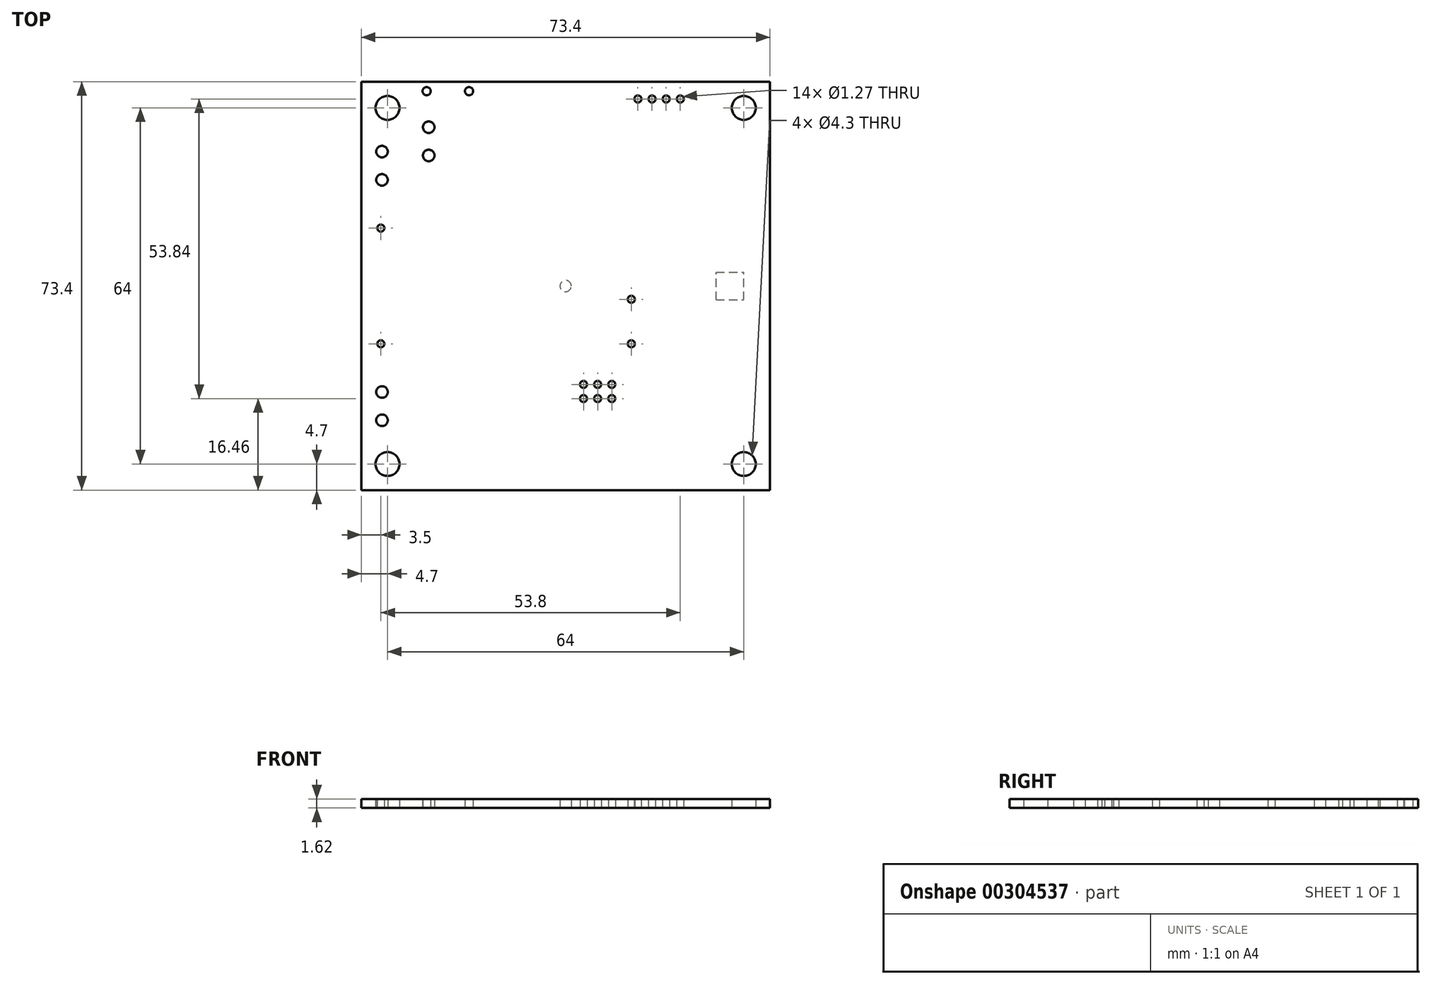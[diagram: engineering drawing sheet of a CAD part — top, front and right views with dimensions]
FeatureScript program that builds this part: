
annotation { "Feature Type Name" : "Feature", "Feature Type Description" : "" }
export const myFeature = defineFeature(function(context is Context, id is Id, definition is map)
    precondition{}
    {
        {
            var Q0;
            Q0=qCreatedBy(makeId("Top.planeOp"),FACE);
            var sketch = newSketch(context, id + "F0", { "sketchPlane" : qUnion([Q0])});
            skLineSegment(sketch, "E0.bottom", {"start": v(36.7, 36.7) * mm, "end": v(-36.7, 36.7) * mm});
            skLineSegment(sketch, "E0.top", {"start": v(36.7, -36.7) * mm, "end": v(-36.7, -36.7) * mm});
            skLineSegment(sketch, "E0.left", {"start": v(36.7, 36.7) * mm, "end": v(36.7, -36.7) * mm});
            skLineSegment(sketch, "E0.right", {"start": v(-36.7, 36.7) * mm, "end": v(-36.7, -36.7) * mm});
            skPoint(sketch, "E0.middle", {"position": v(0, 0) * mm});
            skCircle(sketch, "E1", {"center": v(-32, 32) * mm, "radius": 2.15 * mm});
            skCircle(sketch, "E2", {"center": v(32, 32) * mm, "radius": 2.15 * mm});
            skCircle(sketch, "E3", {"center": v(32, -32) * mm, "radius": 2.15 * mm});
            skCircle(sketch, "E4", {"center": v(-32, -32) * mm, "radius": 2.15 * mm});
            skLineSegment(sketch, "E5.bottom", {"start": v(32, 32) * mm, "end": v(-32, 32) * mm, "construction": true});
            skLineSegment(sketch, "E5.top", {"start": v(32, -32) * mm, "end": v(-32, -32) * mm, "construction": true});
            skLineSegment(sketch, "E5.left", {"start": v(32, 32) * mm, "end": v(32, -32) * mm, "construction": true});
            skLineSegment(sketch, "E5.right", {"start": v(-32, 32) * mm, "end": v(-32, -32) * mm, "construction": true});
            skSolve(sketch);
        }
        {
            var Q0;
            Q0 = qSketchRegion(id + "F0", true);
            extrude(context, id + "F1", {"entities" : qUnion([Q0]), "depth" : 1.57 * mm});
        }
        {
            var Q0;
            Q0=qCreatedBy(makeId("Top.planeOp"),FACE);
            var sketch = newSketch(context, id + "F2", { "sketchPlane" : qUnion([Q0])});
            skLineSegment(sketch, "E6", {"start": v(-33.2, 10.4) * mm, "end": v(-33.2, -10.4) * mm, "construction": true});
            skCircle(sketch, "E7", {"center": v(-33.2, -10.4) * mm, "radius": 0.64 * mm});
            skCircle(sketch, "E8", {"center": v(-33.2, 10.4) * mm, "radius": 0.64 * mm});
            skCircle(sketch, "E9", {"center": v(11.8, -10.4) * mm, "radius": 0.64 * mm});
            skCircle(sketch, "E10", {"center": v(11.8, -2.4) * mm, "radius": 0.64 * mm});
            skLineSegment(sketch, "E11", {"start": v(-33.2, -10.4) * mm, "end": v(11.8, -10.4) * mm, "construction": true});
            skLineSegment(sketch, "E12", {"start": v(11.8, -10.4) * mm, "end": v(11.8, -2.4) * mm, "construction": true});
            skSolve(sketch);
        }
        {
            var Q0;
            Q0 = qSketchRegion(id + "F2", true);
            extrude(context, id + "F3", {"entities" : qUnion([Q0]), "operationType" : NewBodyOperationType.REMOVE, "endBound" : BoundingType.THROUGH_ALL, "depth" : 25.4 * mm});
        }
        {
            var Q0;
            Q0=makeQuery(id+"F1.opExtrude","CAP_FACE",FACE,{"disambiguationData":[OSD([sQuery(id+"F0.wireOp",EDGE,"E0.bottom"),sQuery(id+"F0.wireOp",EDGE,"E0.top"),sQuery(id+"F0.wireOp",EDGE,"E0.left"),sQuery(id+"F0.wireOp",EDGE,"E0.right"),sQuery(id+"F0.wireOp",EDGE,"E1"),sQuery(id+"F0.wireOp",EDGE,"E2"),sQuery(id+"F0.wireOp",EDGE,"E3"),sQuery(id+"F0.wireOp",EDGE,"E4")])],"isStart":true});
            var sketch = newSketch(context, id + "F4", { "sketchPlane" : qUnion([Q0])});
            skLineSegment(sketch, "E13", {"start": v(0, 0) * mm, "end": v(29.53, 0) * mm, "construction": true});
            skLineSegment(sketch, "E14.bottom", {"start": v(27.03, 2.5) * mm, "end": v(32.03, 2.5) * mm});
            skLineSegment(sketch, "E14.top", {"start": v(27.03, -2.5) * mm, "end": v(32.03, -2.5) * mm});
            skLineSegment(sketch, "E14.left", {"start": v(27.03, 2.5) * mm, "end": v(27.03, -2.5) * mm});
            skLineSegment(sketch, "E14.right", {"start": v(32.03, 2.5) * mm, "end": v(32.03, -2.5) * mm});
            skPoint(sketch, "E14.middle", {"position": v(29.53, 0) * mm});
            skSolve(sketch);
        }
        {
            var Q0;
            Q0 = qSketchRegion(id + "F4", true);
            extrude(context, id + "F5", {"entities" : qUnion([Q0]), "operationType" : NewBodyOperationType.ADD, "depth" : 0.05 * mm});
        }
        {
            var Q0;
            Q0=qCreatedBy(makeId("Front.planeOp"),FACE);
            var sketch = newSketch(context, id + "F6", { "sketchPlane" : qUnion([Q0])});
            skLineSegment(sketch, "E15", {"start": v(0, 0) * mm, "end": v(0, -36.38) * mm, "construction": true});
            skSolve(sketch);
        }
        {
            var Q0;
            Q0=qCreatedBy(makeId("Top.planeOp"),FACE);
            var sketch = newSketch(context, id + "F7", { "sketchPlane" : qUnion([Q0])});
            skCircle(sketch, "E16", {"center": v(0, 0) * mm, "radius": 1.02 * mm});
            skSolve(sketch);
        }
        {
            var Q0;
            Q0=qCreatedBy(makeId("Top.planeOp"),FACE);
            var sketch = newSketch(context, id + "F8", { "sketchPlane" : qUnion([Q0])});
            skCircle(sketch, "E17", {"center": v(-24.97, 35) * mm, "radius": 0.74 * mm});
            skCircle(sketch, "E18", {"center": v(-17.35, 35) * mm, "radius": 0.74 * mm});
            skSolve(sketch);
        }
        {
            var Q0;
            Q0 = qSketchRegion(id + "F8", true);
            extrude(context, id + "F9", {"entities" : qUnion([Q0]), "operationType" : NewBodyOperationType.REMOVE, "endBound" : BoundingType.THROUGH_ALL, "depth" : 25.4 * mm});
        }
        {
            var Q0;
            Q0=qCreatedBy(makeId("Top.planeOp"),FACE);
            var sketch = newSketch(context, id + "F10", { "sketchPlane" : qUnion([Q0])});
            skCircle(sketch, "E19", {"center": v(-24.6, 28.53) * mm, "radius": 1.04 * mm});
            skCircle(sketch, "E20", {"center": v(-24.6, 23.45) * mm, "radius": 1.04 * mm});
            skCircle(sketch, "E21", {"center": v(-33, 24.14) * mm, "radius": 1.04 * mm});
            skCircle(sketch, "E22", {"center": v(-33, 19.06) * mm, "radius": 1.04 * mm});
            skCircle(sketch, "E23", {"center": v(-33, -19.06) * mm, "radius": 1.04 * mm});
            skCircle(sketch, "E24", {"center": v(-33, -24.14) * mm, "radius": 1.04 * mm});
            skSolve(sketch);
        }
        {
            var Q0;
            Q0 = qSketchRegion(id + "F10", true);
            extrude(context, id + "F11", {"entities" : qUnion([Q0]), "operationType" : NewBodyOperationType.REMOVE, "endBound" : BoundingType.THROUGH_ALL, "depth" : 25.4 * mm});
        }
        {
            var Q0;
            Q0 = qSketchRegion(id + "F7", true);
            extrude(context, id + "F12", {"entities" : qUnion([Q0]), "operationType" : NewBodyOperationType.REMOVE, "depth" : 1.52 * mm});
        }
        {
            var Q0;
            Q0=qCreatedBy(makeId("Top.planeOp"),FACE);
            var sketch = newSketch(context, id + "F13", { "sketchPlane" : qUnion([Q0])});
            skLineSegment(sketch, "E25", {"start": v(12.98, 33.6) * mm, "end": v(20.6, 33.6) * mm, "construction": true});
            skCircle(sketch, "E26", {"center": v(12.98, 33.6) * mm, "radius": 0.64 * mm});
            skCircle(sketch, "E27", {"center": v(15.52, 33.6) * mm, "radius": 0.64 * mm});
            skCircle(sketch, "E28", {"center": v(18.06, 33.6) * mm, "radius": 0.64 * mm});
            skCircle(sketch, "E29", {"center": v(20.6, 33.6) * mm, "radius": 0.64 * mm});
            skSolve(sketch);
        }
        {
            var Q0;
            Q0 = qSketchRegion(id + "F13", true);
            extrude(context, id + "F14", {"entities" : qUnion([Q0]), "operationType" : NewBodyOperationType.REMOVE, "endBound" : BoundingType.THROUGH_ALL, "depth" : 25.4 * mm});
        }
        {
            var Q0;
            Q0=qCreatedBy(makeId("Top.planeOp"),FACE);
            var sketch = newSketch(context, id + "F15", { "sketchPlane" : qUnion([Q0])});
            skLineSegment(sketch, "E30.bottom", {"start": v(8.3, -20.24) * mm, "end": v(3.22, -20.24) * mm, "construction": true});
            skLineSegment(sketch, "E30.top", {"start": v(8.3, -17.7) * mm, "end": v(3.22, -17.7) * mm, "construction": true});
            skLineSegment(sketch, "E30.left", {"start": v(8.3, -20.24) * mm, "end": v(8.3, -17.7) * mm, "construction": true});
            skLineSegment(sketch, "E30.right", {"start": v(3.22, -20.24) * mm, "end": v(3.22, -17.7) * mm, "construction": true});
            skPoint(sketch, "E30.middle", {"position": v(5.76, -18.97) * mm});
            skLineSegment(sketch, "E31", {"start": v(5.76, -17.7) * mm, "end": v(5.76, -20.24) * mm, "construction": true});
            skCircle(sketch, "E32", {"center": v(3.22, -17.7) * mm, "radius": 0.64 * mm});
            skCircle(sketch, "E33", {"center": v(3.22, -20.24) * mm, "radius": 0.64 * mm});
            skCircle(sketch, "E34", {"center": v(5.76, -20.24) * mm, "radius": 0.64 * mm});
            skCircle(sketch, "E35", {"center": v(5.76, -17.7) * mm, "radius": 0.64 * mm});
            skCircle(sketch, "E36", {"center": v(8.3, -17.7) * mm, "radius": 0.64 * mm});
            skCircle(sketch, "E37", {"center": v(8.3, -20.24) * mm, "radius": 0.64 * mm});
            skSolve(sketch);
        }
        {
            var Q0;
            Q0 = qSketchRegion(id + "F15", true);
            extrude(context, id + "F16", {"entities" : qUnion([Q0]), "operationType" : NewBodyOperationType.REMOVE, "endBound" : BoundingType.THROUGH_ALL, "depth" : 25.4 * mm});
        }
    });
